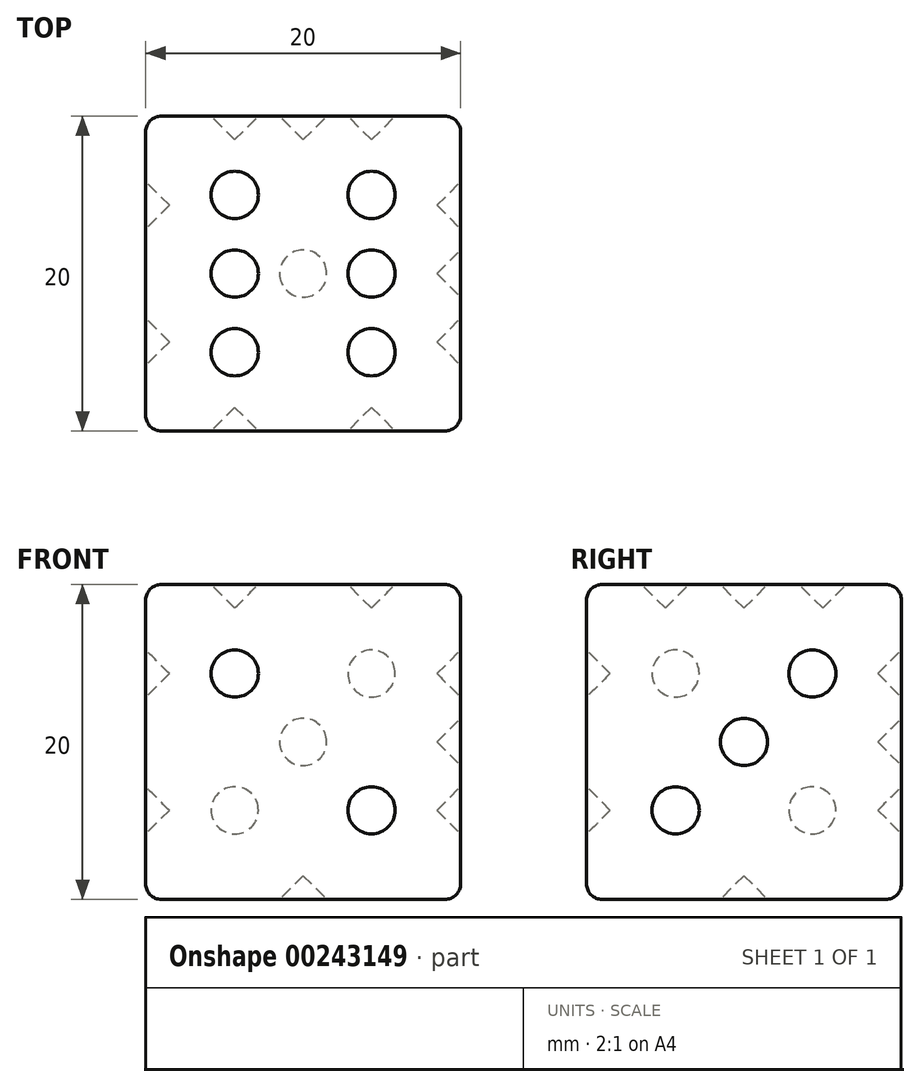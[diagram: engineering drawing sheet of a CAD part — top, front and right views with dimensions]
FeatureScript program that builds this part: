
annotation { "Feature Type Name" : "Feature", "Feature Type Description" : "" }
export const myFeature = defineFeature(function(context is Context, id is Id, definition is map)
    precondition{}
    {
        {
            var Q0;
            Q0=qCreatedBy(makeId("Top.planeOp"),FACE);
            var sketch = newSketch(context, id + "F0", { "sketchPlane" : qUnion([Q0])});
            skLineSegment(sketch, "E0.bottom", {"start": v(20, 20) * mm, "end": v(0, 20) * mm});
            skLineSegment(sketch, "E0.top", {"start": v(20, 0) * mm, "end": v(0, 0) * mm});
            skLineSegment(sketch, "E0.left", {"start": v(20, 20) * mm, "end": v(20, 0) * mm});
            skLineSegment(sketch, "E0.right", {"start": v(0, 20) * mm, "end": v(0, 0) * mm});
            skSolve(sketch);
        }
        {
            var Q0;
            Q0=makeQuery(id+"F0.imprint","IMPRINT",FACE,{"disambiguationData":[TD([[makeQuery(id+"F0.imprint","IMPRINT",EDGE,{"derivedFrom":sQuery(id+"F0.wireOp",EDGE,"E0.bottom")}),1.0]])]});
            extrude(context, id + "F1", {"entities" : qUnion([Q0]), "depth" : 20 * mm});
        }
        {
            var Q0;
            Q0=makeQuery(id+"F1.opExtrude","SWEPT_FACE",FACE,{"disambiguationData":[OSD([sQuery(id+"F0.wireOp",EDGE,"E0.top")])]});
            var sketch = newSketch(context, id + "F2", { "sketchPlane" : qUnion([Q0])});
            skCircle(sketch, "E1", {"center": v(5.66, 14.34) * mm, "radius": 1.5 * mm});
            skCircle(sketch, "E2", {"center": v(14.34, 5.66) * mm, "radius": 1.5 * mm});
            skSolve(sketch);
        }
        {
            var Q0;
            Q0 = qSketchRegion(id + "F2", true);
            extrude(context, id + "F3", {"entities" : qUnion([Q0]), "operationType" : NewBodyOperationType.REMOVE, "oppositeDirection" : true, "depth" : 1.5 * mm});
        }
        {
            var Q0;
            Q0=makeQuery(id+"F1.opExtrude","CAP_EDGE",EDGE,{"disambiguationData":[OSD([sQuery(id+"F0.wireOp",EDGE,"E0.top")])],"isStart":false});
            var Q1;
            Q1=makeQuery(id+"F1.opExtrude","SWEPT_EDGE",EDGE,{"disambiguationData":[OSD([sQuery(id+"F0.wireOp",EDGE,"E0.top"),sQuery(id+"F0.wireOp",EDGE,"E0.left")])]});
            var Q2;
            Q2=makeQuery(id+"F1.opExtrude","CAP_EDGE",EDGE,{"disambiguationData":[OSD([sQuery(id+"F0.wireOp",EDGE,"E0.top")])],"isStart":true});
            var Q3;
            Q3=makeQuery(id+"F1.opExtrude","SWEPT_EDGE",EDGE,{"disambiguationData":[OSD([sQuery(id+"F0.wireOp",EDGE,"E0.top"),sQuery(id+"F0.wireOp",EDGE,"E0.right")])]});
            var Q4;
            Q4=makeQuery(id+"F1.opExtrude","CAP_EDGE",EDGE,{"disambiguationData":[OSD([sQuery(id+"F0.wireOp",EDGE,"E0.left")])],"isStart":true});
            var Q5;
            Q5=makeQuery(id+"F1.opExtrude","CAP_EDGE",EDGE,{"disambiguationData":[OSD([sQuery(id+"F0.wireOp",EDGE,"E0.bottom")])],"isStart":true});
            var Q6;
            Q6=makeQuery(id+"F1.opExtrude","CAP_EDGE",EDGE,{"disambiguationData":[OSD([sQuery(id+"F0.wireOp",EDGE,"E0.right")])],"isStart":true});
            var Q7;
            Q7=makeQuery(id+"F1.opExtrude","SWEPT_EDGE",EDGE,{"disambiguationData":[OSD([sQuery(id+"F0.wireOp",EDGE,"E0.bottom"),sQuery(id+"F0.wireOp",EDGE,"E0.left")])]});
            var Q8;
            Q8=makeQuery(id+"F1.opExtrude","CAP_EDGE",EDGE,{"disambiguationData":[OSD([sQuery(id+"F0.wireOp",EDGE,"E0.left")])],"isStart":false});
            var Q9;
            Q9=makeQuery(id+"F1.opExtrude","CAP_EDGE",EDGE,{"disambiguationData":[OSD([sQuery(id+"F0.wireOp",EDGE,"E0.bottom")])],"isStart":false});
            var Q10;
            Q10=makeQuery(id+"F1.opExtrude","CAP_EDGE",EDGE,{"disambiguationData":[OSD([sQuery(id+"F0.wireOp",EDGE,"E0.right")])],"isStart":false});
            var Q11;
            Q11=makeQuery(id+"F1.opExtrude","SWEPT_EDGE",EDGE,{"disambiguationData":[OSD([sQuery(id+"F0.wireOp",EDGE,"E0.bottom"),sQuery(id+"F0.wireOp",EDGE,"E0.right")])]});
            fillet(context, id + "F4", {"entities" : qUnion([Q0, Q1, Q2, Q3, Q4, Q5, Q6, Q7, Q8, Q9, Q10, Q11]), "radius" : 1 * mm, "tangentPropagation" : true, "allowEdgeOverflow" : false});
        }
        {
            var Q0;
            Q0=makeQuery(id+"F0.imprint","IMPRINT",FACE,{"disambiguationData":[TD([[makeQuery(id+"F0.imprint","IMPRINT",EDGE,{"derivedFrom":sQuery(id+"F0.wireOp",EDGE,"E0.bottom")}),1.0]])]});
            var sketch = newSketch(context, id + "F5", { "sketchPlane" : qUnion([Q0])});
            skLineSegment(sketch, "E3.0", {"start": v(20, 20) * mm, "end": v(0, 20) * mm});
            skLineSegment(sketch, "E3.1", {"start": v(20, 0) * mm, "end": v(0, 0) * mm});
            skCircle(sketch, "E4", {"center": v(10, 10) * mm, "radius": 1.5 * mm});
            skSolve(sketch);
        }
        {
            var Q0;
            Q0 = qSketchRegion(id + "F5", true);
            extrude(context, id + "F6", {"entities" : qUnion([Q0]), "operationType" : NewBodyOperationType.REMOVE, "depth" : 1.5 * mm});
        }
        {
            var Q0;
            Q0=qCreatedBy(makeId("Right.planeOp"),FACE);
            var sketch = newSketch(context, id + "F7", { "sketchPlane" : qUnion([Q0])});
            skCircle(sketch, "E5", {"center": v(5.66, 14.34) * mm, "radius": 1.5 * mm});
            skCircle(sketch, "E6", {"center": v(14.34, 14.34) * mm, "radius": 1.5 * mm});
            skCircle(sketch, "E7", {"center": v(14.34, 5.66) * mm, "radius": 1.5 * mm});
            skCircle(sketch, "E8", {"center": v(5.66, 5.66) * mm, "radius": 1.5 * mm});
            skSolve(sketch);
        }
        {
            var Q0;
            Q0 = qSketchRegion(id + "F7", true);
            extrude(context, id + "F8", {"entities" : qUnion([Q0]), "operationType" : NewBodyOperationType.REMOVE, "depth" : 1.5 * mm});
        }
        {
            var Q0;
            Q0=makeQuery(id+"F3.boolean.opBoolean","COPY",EDGE,{"derivedFrom":makeQuery(id+"F3.opExtrude","CAP_EDGE",EDGE,{"disambiguationData":[OSD([sQuery(id+"F2.wireOp",EDGE,"E1")])],"isStart":false})});
            var Q1;
            Q1=makeQuery(id+"F3.boolean.opBoolean","COPY",EDGE,{"derivedFrom":makeQuery(id+"F3.opExtrude","CAP_EDGE",EDGE,{"disambiguationData":[OSD([sQuery(id+"F2.wireOp",EDGE,"E2")])],"isStart":false})});
            chamfer(context, id + "F9", {"entities" : qUnion([Q0, Q1]), "width" : 1.5 * mm, "tangentPropagation" : true});
        }
        {
            var Q0;
            Q0=makeQuery(id+"F8.boolean.opBoolean","COPY",EDGE,{"derivedFrom":makeQuery(id+"F8.opExtrude","CAP_EDGE",EDGE,{"disambiguationData":[OSD([sQuery(id+"F7.wireOp",EDGE,"E6")])],"isStart":false})});
            var Q1;
            Q1=makeQuery(id+"F8.boolean.opBoolean","COPY",EDGE,{"derivedFrom":makeQuery(id+"F8.opExtrude","CAP_EDGE",EDGE,{"disambiguationData":[OSD([sQuery(id+"F7.wireOp",EDGE,"E5")])],"isStart":false})});
            var Q2;
            Q2=makeQuery(id+"F8.boolean.opBoolean","COPY",EDGE,{"derivedFrom":makeQuery(id+"F8.opExtrude","CAP_EDGE",EDGE,{"disambiguationData":[OSD([sQuery(id+"F7.wireOp",EDGE,"E8")])],"isStart":false})});
            var Q3;
            Q3=makeQuery(id+"F8.boolean.opBoolean","COPY",EDGE,{"derivedFrom":makeQuery(id+"F8.opExtrude","CAP_EDGE",EDGE,{"disambiguationData":[OSD([sQuery(id+"F7.wireOp",EDGE,"E7")])],"isStart":false})});
            chamfer(context, id + "F10", {"entities" : qUnion([Q0, Q1, Q2, Q3]), "width" : 1.5 * mm, "tangentPropagation" : true});
        }
        {
            var Q0;
            Q0=makeQuery(id+"F6.boolean.opBoolean","COPY",EDGE,{"derivedFrom":makeQuery(id+"F6.opExtrude","CAP_EDGE",EDGE,{"disambiguationData":[OSD([sQuery(id+"F5.wireOp",EDGE,"E4")])],"isStart":false})});
            chamfer(context, id + "F11", {"entities" : qUnion([Q0]), "width" : 1.5 * mm, "tangentPropagation" : true});
        }
        {
            var Q0;
            Q0=makeQuery(id+"F1.opExtrude","SWEPT_FACE",FACE,{"disambiguationData":[OSD([sQuery(id+"F0.wireOp",EDGE,"E0.left")])]});
            var sketch = newSketch(context, id + "F12", { "sketchPlane" : qUnion([Q0])});
            skLineSegment(sketch, "E9.0", {"start": v(20, 20) * mm, "end": v(0, 20) * mm});
            skLineSegment(sketch, "E10.0", {"start": v(20, 0) * mm, "end": v(0, 0) * mm});
            skCircle(sketch, "E11", {"center": v(5.66, 5.66) * mm, "radius": 1.5 * mm});
            skCircle(sketch, "E12", {"center": v(10, 10) * mm, "radius": 1.5 * mm});
            skCircle(sketch, "E13", {"center": v(14.34, 14.34) * mm, "radius": 1.5 * mm});
            skSolve(sketch);
        }
        {
            var Q0;
            Q0 = qSketchRegion(id + "F12", true);
            extrude(context, id + "F13", {"entities" : qUnion([Q0]), "operationType" : NewBodyOperationType.REMOVE, "oppositeDirection" : true, "depth" : 1.5 * mm});
        }
        {
            var Q0;
            Q0=makeQuery(id+"F13.boolean.opBoolean","COPY",FACE,{"derivedFrom":makeQuery(id+"F13.opExtrude","CAP_FACE",FACE,{"disambiguationData":[OSD([sQuery(id+"F12.wireOp",EDGE,"E12")])],"isStart":false})});
            var Q1;
            Q1=makeQuery(id+"F13.boolean.opBoolean","COPY",EDGE,{"derivedFrom":makeQuery(id+"F13.opExtrude","CAP_EDGE",EDGE,{"disambiguationData":[OSD([sQuery(id+"F12.wireOp",EDGE,"E13")])],"isStart":false})});
            var Q2;
            Q2=makeQuery(id+"F13.boolean.opBoolean","COPY",EDGE,{"derivedFrom":makeQuery(id+"F13.opExtrude","CAP_EDGE",EDGE,{"disambiguationData":[OSD([sQuery(id+"F12.wireOp",EDGE,"E11")])],"isStart":false})});
            chamfer(context, id + "F14", {"entities" : qUnion([Q0, Q1, Q2]), "width" : 1.5 * mm, "tangentPropagation" : true});
        }
        {
            var Q0;
            Q0=makeQuery(id+"F1.opExtrude","SWEPT_FACE",FACE,{"disambiguationData":[OSD([sQuery(id+"F0.wireOp",EDGE,"E0.bottom")])]});
            var sketch = newSketch(context, id + "F15", { "sketchPlane" : qUnion([Q0])});
            skLineSegment(sketch, "E14.0", {"start": v(-20, 20) * mm, "end": v(0, 20) * mm});
            skLineSegment(sketch, "E15.0", {"start": v(-20, 0) * mm, "end": v(0, 0) * mm});
            skCircle(sketch, "E16", {"center": v(-14.34, 14.34) * mm, "radius": 1.5 * mm});
            skCircle(sketch, "E17", {"center": v(-5.66, 5.66) * mm, "radius": 1.5 * mm});
            skCircle(sketch, "E18", {"center": v(-14.34, 5.66) * mm, "radius": 1.5 * mm});
            skCircle(sketch, "E19", {"center": v(-5.66, 14.34) * mm, "radius": 1.5 * mm});
            skCircle(sketch, "E20", {"center": v(-10, 10) * mm, "radius": 1.5 * mm});
            skSolve(sketch);
        }
        {
            var Q0;
            Q0 = qSketchRegion(id + "F15", true);
            extrude(context, id + "F16", {"entities" : qUnion([Q0]), "operationType" : NewBodyOperationType.REMOVE, "oppositeDirection" : true, "depth" : 1.5 * mm});
        }
        {
            var Q0;
            Q0=makeQuery(id+"F16.boolean.opBoolean","COPY",EDGE,{"derivedFrom":makeQuery(id+"F16.opExtrude","CAP_EDGE",EDGE,{"disambiguationData":[OSD([sQuery(id+"F15.wireOp",EDGE,"E16")])],"isStart":false})});
            var Q1;
            Q1=makeQuery(id+"F16.boolean.opBoolean","COPY",EDGE,{"derivedFrom":makeQuery(id+"F16.opExtrude","CAP_EDGE",EDGE,{"disambiguationData":[OSD([sQuery(id+"F15.wireOp",EDGE,"E19")])],"isStart":false})});
            var Q2;
            Q2=makeQuery(id+"F16.boolean.opBoolean","COPY",EDGE,{"derivedFrom":makeQuery(id+"F16.opExtrude","CAP_EDGE",EDGE,{"disambiguationData":[OSD([sQuery(id+"F15.wireOp",EDGE,"E20")])],"isStart":false})});
            var Q3;
            Q3=makeQuery(id+"F16.boolean.opBoolean","COPY",EDGE,{"derivedFrom":makeQuery(id+"F16.opExtrude","CAP_EDGE",EDGE,{"disambiguationData":[OSD([sQuery(id+"F15.wireOp",EDGE,"E18")])],"isStart":false})});
            var Q4;
            Q4=makeQuery(id+"F16.boolean.opBoolean","COPY",EDGE,{"derivedFrom":makeQuery(id+"F16.opExtrude","CAP_EDGE",EDGE,{"disambiguationData":[OSD([sQuery(id+"F15.wireOp",EDGE,"E17")])],"isStart":false})});
            chamfer(context, id + "F17", {"entities" : qUnion([Q0, Q1, Q2, Q3, Q4]), "width" : 1.5 * mm, "tangentPropagation" : true});
        }
        {
            var Q0;
            Q0=makeQuery(id+"F1.opExtrude","CAP_FACE",FACE,{"disambiguationData":[OSD([sQuery(id+"F0.wireOp",EDGE,"E0.bottom"),sQuery(id+"F0.wireOp",EDGE,"E0.top"),sQuery(id+"F0.wireOp",EDGE,"E0.left"),sQuery(id+"F0.wireOp",EDGE,"E0.right")])],"isStart":false});
            var sketch = newSketch(context, id + "F18", { "sketchPlane" : qUnion([Q0])});
            skLineSegment(sketch, "E21.0", {"start": v(20, 20) * mm, "end": v(0, 20) * mm});
            skLineSegment(sketch, "E22.0", {"start": v(20, 0) * mm, "end": v(0, 0) * mm});
            skLineSegment(sketch, "E23", {"start": v(14.34, 5) * mm, "end": v(14.34, 0) * mm});
            skLineSegment(sketch, "E24", {"start": v(5.66, 15) * mm, "end": v(5.66, 10) * mm});
            skLineSegment(sketch, "E25", {"start": v(5.66, 10) * mm, "end": v(5.66, 5) * mm});
            skLineSegment(sketch, "E26", {"start": v(5.66, 5) * mm, "end": v(5.66, 0) * mm});
            skLineSegment(sketch, "E27", {"start": v(14.34, 5) * mm, "end": v(14.34, 10) * mm});
            skLineSegment(sketch, "E28", {"start": v(14.34, 10) * mm, "end": v(14.34, 15) * mm});
            skLineSegment(sketch, "E29", {"start": v(14.34, 15) * mm, "end": v(14.34, 20) * mm});
            skCircle(sketch, "E30", {"center": v(5.66, 15) * mm, "radius": 1.5 * mm});
            skCircle(sketch, "E31", {"center": v(5.66, 10) * mm, "radius": 1.5 * mm});
            skCircle(sketch, "E32", {"center": v(5.66, 5) * mm, "radius": 1.5 * mm});
            skCircle(sketch, "E33", {"center": v(14.34, 15) * mm, "radius": 1.5 * mm});
            skCircle(sketch, "E34", {"center": v(14.34, 10) * mm, "radius": 1.5 * mm});
            skCircle(sketch, "E35", {"center": v(14.34, 5) * mm, "radius": 1.5 * mm});
            skSolve(sketch);
        }
        {
            var Q0;
            Q0 = qSketchRegion(id + "F18", true);
            extrude(context, id + "F19", {"entities" : qUnion([Q0]), "operationType" : NewBodyOperationType.REMOVE, "oppositeDirection" : true, "depth" : 1.5 * mm});
        }
        {
            var Q0;
            Q0=makeQuery(id+"F19.boolean.opBoolean","COPY",EDGE,{"derivedFrom":makeQuery(id+"F19.opExtrude","CAP_EDGE",EDGE,{"disambiguationData":[OSD([sQuery(id+"F18.wireOp",EDGE,"E32")])],"isStart":false})});
            var Q1;
            Q1=makeQuery(id+"F19.boolean.opBoolean","COPY",EDGE,{"derivedFrom":makeQuery(id+"F19.opExtrude","CAP_EDGE",EDGE,{"disambiguationData":[OSD([sQuery(id+"F18.wireOp",EDGE,"E31")])],"isStart":false})});
            var Q2;
            Q2=makeQuery(id+"F19.boolean.opBoolean","COPY",EDGE,{"derivedFrom":makeQuery(id+"F19.opExtrude","CAP_EDGE",EDGE,{"disambiguationData":[OSD([sQuery(id+"F18.wireOp",EDGE,"E30")])],"isStart":false})});
            var Q3;
            Q3=makeQuery(id+"F19.boolean.opBoolean","COPY",FACE,{"derivedFrom":makeQuery(id+"F19.opExtrude","CAP_FACE",FACE,{"disambiguationData":[OSD([sQuery(id+"F18.wireOp",EDGE,"E33")])],"isStart":false})});
            var Q4;
            Q4=makeQuery(id+"F19.boolean.opBoolean","COPY",EDGE,{"derivedFrom":makeQuery(id+"F19.opExtrude","CAP_EDGE",EDGE,{"disambiguationData":[OSD([sQuery(id+"F18.wireOp",EDGE,"E35")])],"isStart":false})});
            var Q5;
            Q5=makeQuery(id+"F19.boolean.opBoolean","COPY",EDGE,{"derivedFrom":makeQuery(id+"F19.opExtrude","CAP_EDGE",EDGE,{"disambiguationData":[OSD([sQuery(id+"F18.wireOp",EDGE,"E34")])],"isStart":false})});
            chamfer(context, id + "F20", {"entities" : qUnion([Q0, Q1, Q2, Q3, Q4, Q5]), "width" : 1.5 * mm, "tangentPropagation" : true});
        }
    });
